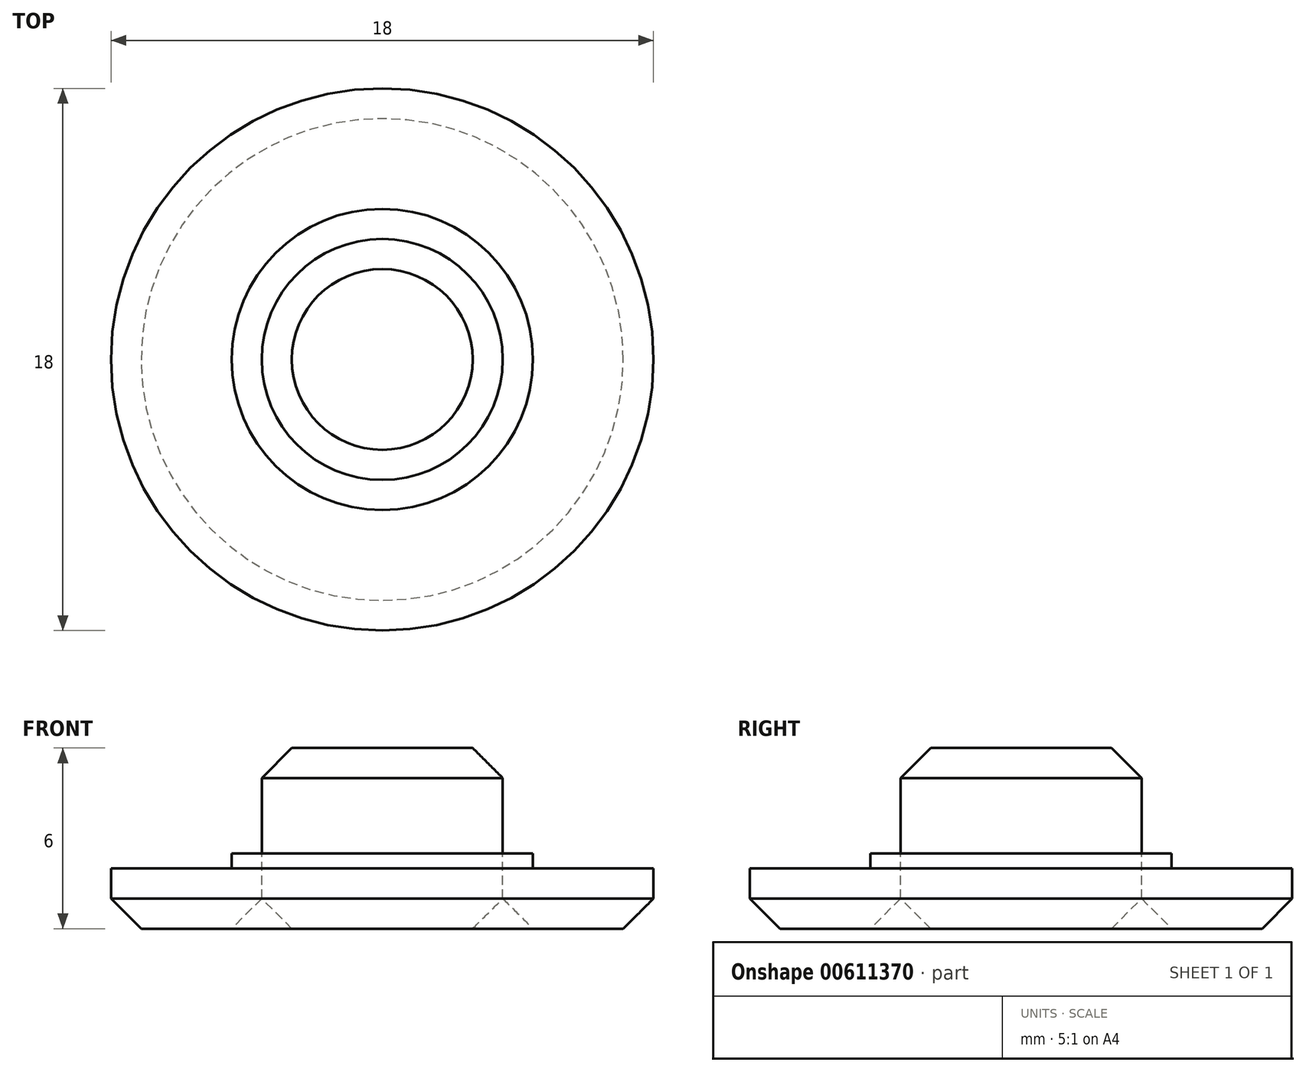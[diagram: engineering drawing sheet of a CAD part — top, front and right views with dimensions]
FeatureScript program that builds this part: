
annotation { "Feature Type Name" : "Feature", "Feature Type Description" : "" }
export const myFeature = defineFeature(function(context is Context, id is Id, definition is map)
    precondition{}
    {
        {
            var Q0;
            Q0=qCreatedBy(makeId("Top.planeOp"),FACE);
            var sketch = newSketch(context, id + "F0", { "sketchPlane" : qUnion([Q0])});
            skCircle(sketch, "E0", {"center": v(0, 0) * mm, "radius": 9 * mm});
            skCircle(sketch, "E1", {"center": v(0, 0) * mm, "radius": 5 * mm});
            skCircle(sketch, "E2", {"center": v(0, 0) * mm, "radius": 4 * mm});
            skSolve(sketch);
        }
        {
            var Q0;
            Q0=makeQuery(id+"F0.imprint","IMPRINT",FACE,{"disambiguationData":[TD([[makeQuery(id+"F0.imprint","IMPRINT",EDGE,{"derivedFrom":sQuery(id+"F0.wireOp",EDGE,"E0")}),1.0]])]});
            var Q1;
            Q1=sQuery(id+"F0.wireOp",EDGE,"E0");
            extrude(context, id + "F1", {"entities" : qUnion([Q0]), "surfaceEntities" : qUnion([Q1]), "depth" : 2 * mm, "offsetDistance" : 25 * mm});
        }
        {
            var Q0;
            Q0=makeQuery(id+"F0.imprint","IMPRINT",FACE,{"disambiguationData":[TD([[makeQuery(id+"F0.imprint","IMPRINT",EDGE,{"derivedFrom":sQuery(id+"F0.wireOp",EDGE,"E1")}),1.0]])]});
            var Q1;
            Q1=sQuery(id+"F0.wireOp",EDGE,"E1");
            var Q2;
            Q2=sQuery(id+"F0.wireOp",EDGE,"E2");
            extrude(context, id + "F2", {"entities" : qUnion([Q0]), "operationType" : NewBodyOperationType.ADD, "surfaceEntities" : qUnion([Q1, Q2]), "depth" : 2.5 * mm, "offsetDistance" : 25 * mm});
        }
        {
            var Q0;
            Q0=makeQuery(id+"F2.opExtrude","CAP_FACE",FACE,{"disambiguationData":[OSD([sQuery(id+"F0.wireOp",EDGE,"E1"),sQuery(id+"F0.wireOp",EDGE,"E2")])],"isStart":false});
            var sketch = newSketch(context, id + "F3", { "sketchPlane" : qUnion([Q0])});
            skCircle(sketch, "E3", {"center": v(0, 0) * mm, "radius": 4 * mm});
            skSolve(sketch);
        }
        {
            var Q0;
            Q0 = qSketchRegion(id + "F3", true);
            extrude(context, id + "F4", {"entities" : qUnion([Q0]), "depth" : 3.5 * mm, "offsetDistance" : 25 * mm});
        }
        {
            var Q0;
            Q0 = qSketchRegion(id + "F3", true);
            extrude(context, id + "F5", {"entities" : qUnion([Q0]), "oppositeDirection" : true, "depth" : 2.5 * mm, "offsetDistance" : 25 * mm});
        }
        {
            var Q0;
            Q0=makeQuery(id+"F2.opExtrude","CAP_EDGE",EDGE,{"disambiguationData":[OSD([sQuery(id+"F0.wireOp",EDGE,"E2")])],"isStart":true});
            chamfer(context, id + "F6", {"entities" : qUnion([Q0]), "width" : 1 * mm, "tangentPropagation" : true});
        }
        {
            var Q0;
            Q0=makeQuery(id+"F5.opExtrude","CAP_FACE",FACE,{"disambiguationData":[OSD([sQuery(id+"F3.wireOp",EDGE,"E3")])],"isStart":false});
            var Q1;
            Q1=makeQuery(id+"F1.opExtrude","CAP_EDGE",EDGE,{"disambiguationData":[OSD([sQuery(id+"F0.wireOp",EDGE,"E0")])],"isStart":true});
            var Q2;
            Q2=makeQuery(id+"F4.opExtrude","CAP_EDGE",EDGE,{"disambiguationData":[OSD([sQuery(id+"F3.wireOp",EDGE,"E3")])],"isStart":false});
            chamfer(context, id + "F7", {"entities" : qUnion([Q0, Q1, Q2]), "width" : 1 * mm, "tangentPropagation" : true});
        }
    });
